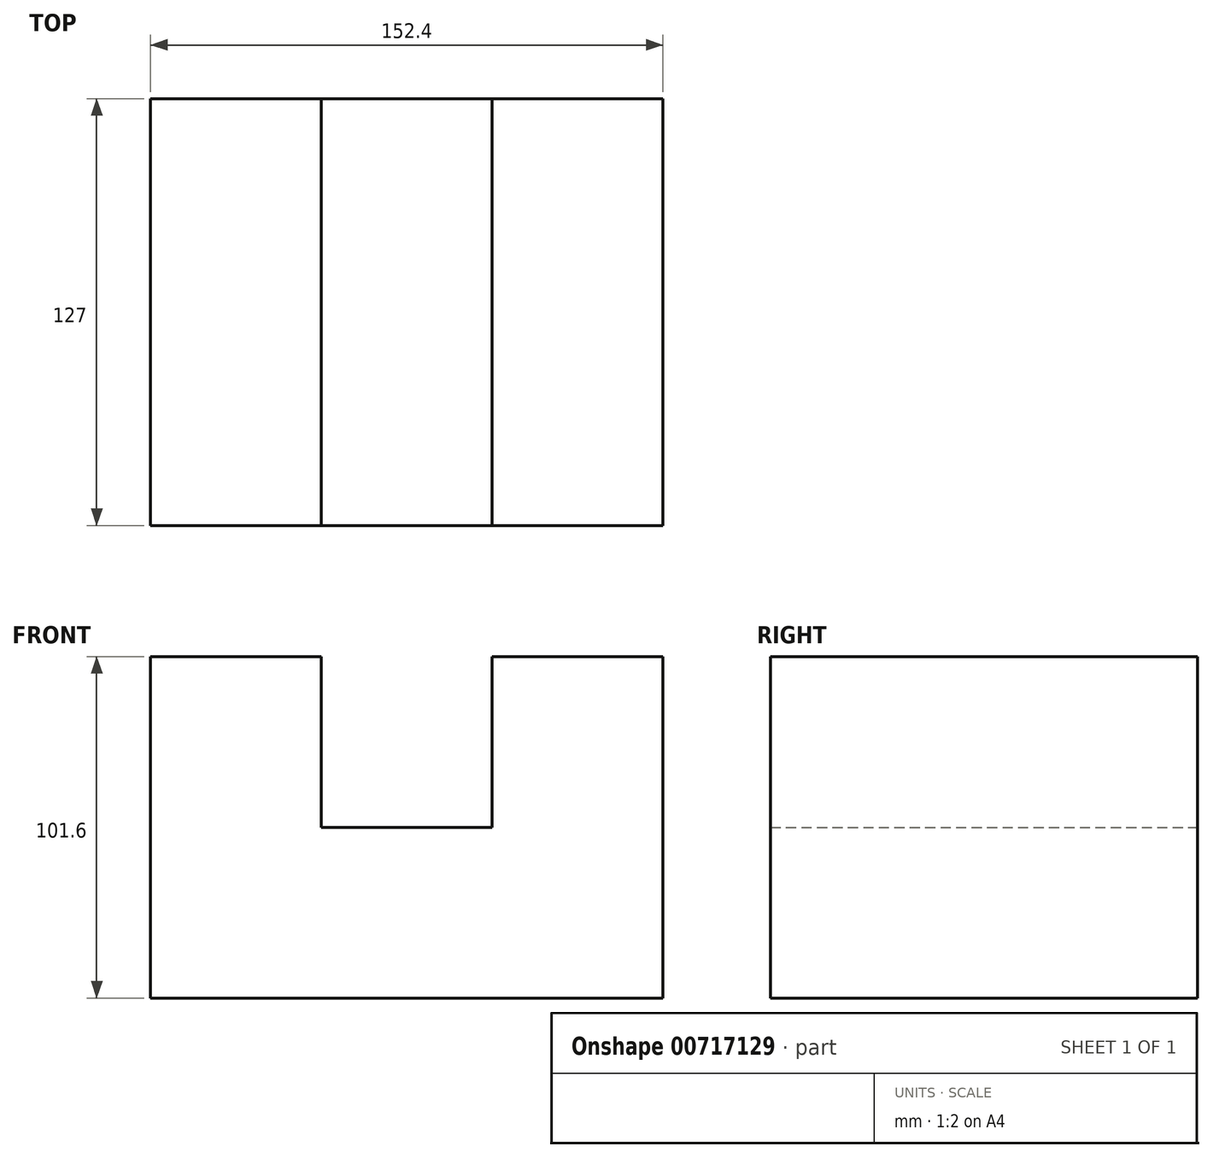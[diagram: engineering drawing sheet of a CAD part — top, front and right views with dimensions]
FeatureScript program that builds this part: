
annotation { "Feature Type Name" : "Feature", "Feature Type Description" : "" }
export const myFeature = defineFeature(function(context is Context, id is Id, definition is map)
    precondition{}
    {
        {
            var Q0;
            Q0=qCreatedBy(makeId("Front.planeOp"),FACE);
            var sketch = newSketch(context, id + "F0", { "sketchPlane" : qUnion([Q0])});
            skLineSegment(sketch, "E0", {"start": v(-68.96, -40.14) * mm, "end": v(83.44, -40.14) * mm});
            skLineSegment(sketch, "E1", {"start": v(83.44, -40.14) * mm, "end": v(83.44, 61.46) * mm});
            skLineSegment(sketch, "E2", {"start": v(83.44, 61.46) * mm, "end": v(32.64, 61.46) * mm});
            skLineSegment(sketch, "E3", {"start": v(32.64, 61.46) * mm, "end": v(32.64, 10.66) * mm});
            skLineSegment(sketch, "E4", {"start": v(32.64, 10.66) * mm, "end": v(-18.16, 10.66) * mm});
            skLineSegment(sketch, "E5", {"start": v(-18.16, 10.66) * mm, "end": v(-18.16, 61.46) * mm});
            skLineSegment(sketch, "E6", {"start": v(-18.16, 61.46) * mm, "end": v(-68.96, 61.46) * mm});
            skLineSegment(sketch, "E7", {"start": v(-68.96, 61.46) * mm, "end": v(-68.96, -40.14) * mm});
            skSolve(sketch);
        }
        {
            var Q0;
            Q0=makeQuery(id+"F0.imprint","IMPRINT",FACE,{"disambiguationData":[TD([[makeQuery(id+"F0.imprint","IMPRINT",EDGE,{"derivedFrom":sQuery(id+"F0.wireOp",EDGE,"E0")}),1.0]])]});
            extrude(context, id + "F1", {"entities" : qUnion([Q0]), "depth" : 127 * mm, "offsetDistance" : 25.4 * mm});
        }
    });
